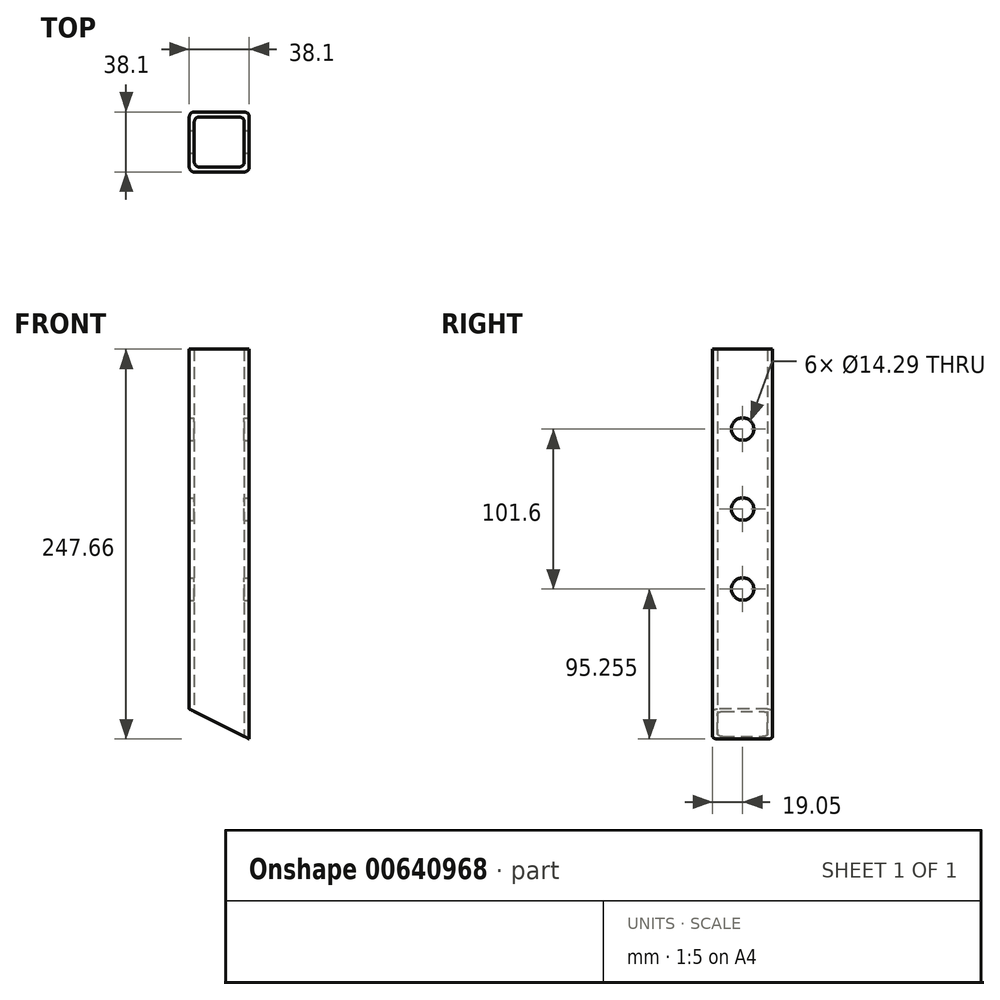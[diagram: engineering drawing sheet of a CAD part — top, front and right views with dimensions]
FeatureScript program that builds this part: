
annotation { "Feature Type Name" : "Feature", "Feature Type Description" : "" }
export const myFeature = defineFeature(function(context is Context, id is Id, definition is map)
    precondition{}
    {
        {
            var Q0;
            Q0=qCreatedBy(makeId("Top.planeOp"),FACE);
            var sketch = newSketch(context, id + "F0", { "sketchPlane" : qUnion([Q0])});
            skLineSegment(sketch, "E0.bottom", {"start": v(-19.05, 19.05) * mm, "end": v(19.05, 19.05) * mm});
            skLineSegment(sketch, "E0.top", {"start": v(-19.05, -19.05) * mm, "end": v(19.05, -19.05) * mm});
            skLineSegment(sketch, "E0.left", {"start": v(-19.05, 19.05) * mm, "end": v(-19.05, -19.05) * mm});
            skLineSegment(sketch, "E0.right", {"start": v(19.05, 19.05) * mm, "end": v(19.05, -19.05) * mm});
            skSolve(sketch);
        }
        {
            var Q0;
            Q0=makeQuery(id+"F0.imprint","IMPRINT",FACE,{"disambiguationData":[TD([[makeQuery(id+"F0.imprint","IMPRINT",EDGE,{"derivedFrom":sQuery(id+"F0.wireOp",EDGE,"E0.bottom")}),-1.0]])]});
            extrude(context, id + "F1", {"entities" : qUnion([Q0]), "endBound" : BoundingType.SYMMETRIC, "depth" : 247.65 * mm, "offsetDistance" : 25.4 * mm});
        }
        {
            var Q0;
            Q0=makeQuery(id+"F1.opExtrude","CAP_FACE",FACE,{"disambiguationData":[OSD([sQuery(id+"F0.wireOp",EDGE,"E0.bottom"),sQuery(id+"F0.wireOp",EDGE,"E0.top"),sQuery(id+"F0.wireOp",EDGE,"E0.left"),sQuery(id+"F0.wireOp",EDGE,"E0.right")])],"isStart":false});
            var Q1;
            Q1=makeQuery(id+"F1.opExtrude","CAP_FACE",FACE,{"disambiguationData":[OSD([sQuery(id+"F0.wireOp",EDGE,"E0.bottom"),sQuery(id+"F0.wireOp",EDGE,"E0.top"),sQuery(id+"F0.wireOp",EDGE,"E0.left"),sQuery(id+"F0.wireOp",EDGE,"E0.right")])],"isStart":true});
            shell(context, id + "F2", {"entities" : qUnion([Q0, Q1]), "thickness" : 3.17 * mm});
        }
        {
            var Q0;
            Q0=makeQuery(id+"F1.opExtrude","SWEPT_FACE",FACE,{"disambiguationData":[OSD([sQuery(id+"F0.wireOp",EDGE,"E0.right")])]});
            var sketch = newSketch(context, id + "F3", { "sketchPlane" : qUnion([Q0])});
            skCircle(sketch, "E1", {"center": v(0, 73.03) * mm, "radius": 7.14 * mm});
            skCircle(sketch, "E2", {"center": v(0, 22.23) * mm, "radius": 7.14 * mm});
            skCircle(sketch, "E3", {"center": v(0, -28.58) * mm, "radius": 7.14 * mm});
            skSolve(sketch);
        }
        {
            var Q0;
            Q0=makeQuery(id+"F3.imprint","IMPRINT",FACE,{"disambiguationData":[TD([[makeQuery(id+"F3.imprint","IMPRINT",EDGE,{"derivedFrom":sQuery(id+"F3.wireOp",EDGE,"E1")}),1.0]])]});
            var Q1;
            Q1=makeQuery(id+"F3.imprint","IMPRINT",FACE,{"disambiguationData":[TD([[makeQuery(id+"F3.imprint","IMPRINT",EDGE,{"derivedFrom":sQuery(id+"F3.wireOp",EDGE,"E2")}),1.0]])]});
            var Q2;
            Q2=makeQuery(id+"F3.imprint","IMPRINT",FACE,{"disambiguationData":[TD([[makeQuery(id+"F3.imprint","IMPRINT",EDGE,{"derivedFrom":sQuery(id+"F3.wireOp",EDGE,"E3")}),1.0]])]});
            extrude(context, id + "F4", {"entities" : qUnion([Q0, Q1, Q2]), "operationType" : NewBodyOperationType.REMOVE, "endBound" : BoundingType.THROUGH_ALL, "oppositeDirection" : true, "depth" : 25.4 * mm, "offsetDistance" : 25.4 * mm});
        }
        {
            var Q0;
            Q0=makeQuery(id+"F1.opExtrude","SWEPT_FACE",FACE,{"disambiguationData":[OSD([sQuery(id+"F0.wireOp",EDGE,"E0.top")])]});
            var sketch = newSketch(context, id + "F5", { "sketchPlane" : qUnion([Q0])});
            skLineSegment(sketch, "E4", {"start": v(19.05, -123.83) * mm, "end": v(-19.05, -123.83) * mm});
            skLineSegment(sketch, "E5", {"start": v(-19.05, -123.83) * mm, "end": v(-19.05, -104.77) * mm});
            skLineSegment(sketch, "E6", {"start": v(-19.05, -104.77) * mm, "end": v(19.05, -123.83) * mm});
            skSolve(sketch);
        }
        {
            var Q0;
            Q0 = qSketchRegion(id + "F5", true);
            extrude(context, id + "F6", {"entities" : qUnion([Q0]), "operationType" : NewBodyOperationType.REMOVE, "endBound" : BoundingType.THROUGH_ALL, "oppositeDirection" : true, "depth" : 25.4 * mm, "offsetDistance" : 25.4 * mm});
        }
        {
            var Q0;
            Q0=makeQuery(id+"F1.opExtrude","SWEPT_EDGE",EDGE,{"disambiguationData":[OSD([sQuery(id+"F0.wireOp",EDGE,"E0.top"),sQuery(id+"F0.wireOp",EDGE,"E0.left")])]});
            var Q1;
            Q1=makeQuery(id+"F1.opExtrude","SWEPT_EDGE",EDGE,{"disambiguationData":[OSD([sQuery(id+"F0.wireOp",EDGE,"E0.bottom"),sQuery(id+"F0.wireOp",EDGE,"E0.right")])]});
            var Q2;
            Q2=makeQuery(id+"F1.opExtrude","SWEPT_EDGE",EDGE,{"disambiguationData":[OSD([sQuery(id+"F0.wireOp",EDGE,"E0.top"),sQuery(id+"F0.wireOp",EDGE,"E0.right")])]});
            var Q3;
            Q3=makeQuery(id+"F1.opExtrude","SWEPT_EDGE",EDGE,{"disambiguationData":[OSD([sQuery(id+"F0.wireOp",EDGE,"E0.bottom"),sQuery(id+"F0.wireOp",EDGE,"E0.left")])]});
            var Q4;
            Q4=makeQuery(id+"F2.opShell","OFFSET_EDGE",EDGE,{"disambiguationData":[OSD([sQuery(id+"F0.wireOp",EDGE,"E0.top"),sQuery(id+"F0.wireOp",EDGE,"E0.left")])]});
            var Q5;
            Q5=makeQuery(id+"F2.opShell","OFFSET_EDGE",EDGE,{"disambiguationData":[OSD([sQuery(id+"F0.wireOp",EDGE,"E0.bottom"),sQuery(id+"F0.wireOp",EDGE,"E0.left")])]});
            var Q6;
            Q6=makeQuery(id+"F2.opShell","OFFSET_EDGE",EDGE,{"disambiguationData":[OSD([sQuery(id+"F0.wireOp",EDGE,"E0.bottom"),sQuery(id+"F0.wireOp",EDGE,"E0.right")])]});
            var Q7;
            Q7=makeQuery(id+"F2.opShell","OFFSET_EDGE",EDGE,{"disambiguationData":[OSD([sQuery(id+"F0.wireOp",EDGE,"E0.top"),sQuery(id+"F0.wireOp",EDGE,"E0.right")])]});
            fillet(context, id + "F7", {"entities" : qUnion([Q0, Q1, Q2, Q3, Q4, Q5, Q6, Q7]), "radius" : 3.17 * mm, "tangentPropagation" : true, "allowEdgeOverflow" : false});
        }
    });
